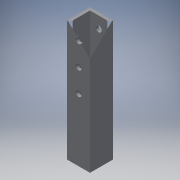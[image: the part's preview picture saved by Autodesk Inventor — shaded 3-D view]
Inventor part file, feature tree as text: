
AUTODESK INVENTOR PART (.ipt)
format: ipt  version: 2016 (Build 200138000, 138)  size: 134,656 bytes
history: native  units: in
note: dims shown in document units (in); Inventor stores cm internally (conversion verified against a paired STEP export)
features: extrude x3, sketch x3
ambient origin geometry x8: Origin, YZ Plane, XZ Plane, XY Plane, X Axis, Y Axis, Z Axis, Center Point
bodies: Solid1 (feature_tree)
feature tree (6):
  extrude  "Extrusion1"  Depth=1.0in
  extrude  "Extrusion2"  Depth=4.247in TaperAngle=0.0deg
  extrude  "Extrusion3"  Depth=1.0in
  sketch  "Sketch1"  dims[d0=1.0in d1=1.0in]
  sketch  "Sketch2"  dims[d2=0.125in d3=4.247in d4=0.0in]
  sketch  "Sketch3"  dims[d5=0.2656in d6=0.5in d7=0.5in d8=0.2656in d9=0.5in d10=1.0in d11=0.2656in d12=1.0in d13=0.5in d14=1.0in d15=0.0in d16=0.2656in d17=0.5in d18=0.5in d19=0.5in d20=1.5in d21=1.0in d22=0.0in]
